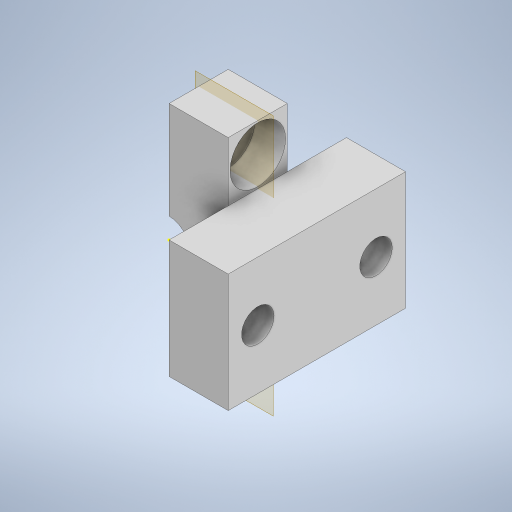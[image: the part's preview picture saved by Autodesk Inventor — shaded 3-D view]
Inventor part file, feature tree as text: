
AUTODESK INVENTOR PART (.ipt)
format: ipt  version: 2023 (Build 270158000, 158)  size: 345,088 bytes
history: native  units: mm
features: sketch x10, extrude x9, plane x1
ambient origin geometry x8: Origin, YZ Plane, XZ Plane, XY Plane, X Axis, Y Axis, Z Axis, Center Point
bodies: Solid1 (feature_tree)
feature tree (20):
  extrude  "Extrusion1"  Depth=20.0mm
  plane  "Work Plane1"
  extrude  "Extrusion2"  Depth=5.0mm
  extrude  "Extrusion3"  Depth=1.8mm
  extrude  "Extrusion4"  Depth=2.5mm
  extrude  "Extrusion5"  Depth=2.5mm
  sketch  "Sketch6"  dims[d21=2.5mm d22=2.7mm]
  extrude  "Extrusion6"  Depth=2.5mm
  extrude  "Extrusion7"  Depth=25.0mm TaperAngle=0.0deg
  extrude  "Extrusion8"  Depth=4.0mm
  extrude  "Extrusion9"  Depth=5.0mm
  sketch  "Sketch1"  dims[d0=20.0mm d1=20.0mm]
  sketch  "Sketch2"  dims[d10=5.0mm d11=0.0mm d12=5.0mm]
  sketch  "Sketch3"  dims[d13=1.8mm d14=0.0mm d15=3.5mm]
  sketch  "Sketch4"  dims[d16=8.0mm d17=0.0mm d18=2.5mm]
  sketch  "Sketch5"  dims[d19=2.5mm d20=2.5mm]
  sketch  "Sketch7"  dims[d23=2.7mm d24=25.0mm d25=0.0mm]
  sketch  "Sketch8"  dims[d26=4.0mm d27=4.0mm]
  sketch  "Sketch9"  dims[d28=4.0mm d29=0.0mm d30=5.0mm]
  sketch  "Sketch10"  dims[d31=5.0mm d32=5.0mm d33=5.0mm d34=10.0mm d35=0.0mm d36=5.0mm d37=5.0mm d38=5.0mm d39=2.75mm d40=2.75mm d41=5.0mm d42=5.0mm d43=5.0mm d44=5.0mm d45=2.5mm d46=2.5mm d47=5.0mm d48=0.0mm d49=4.0mm d50=4.0mm d51=2.0mm d52=0.0mm d53=4.7mm d54=4.7mm d55=2.6mm d56=0.0mm]
